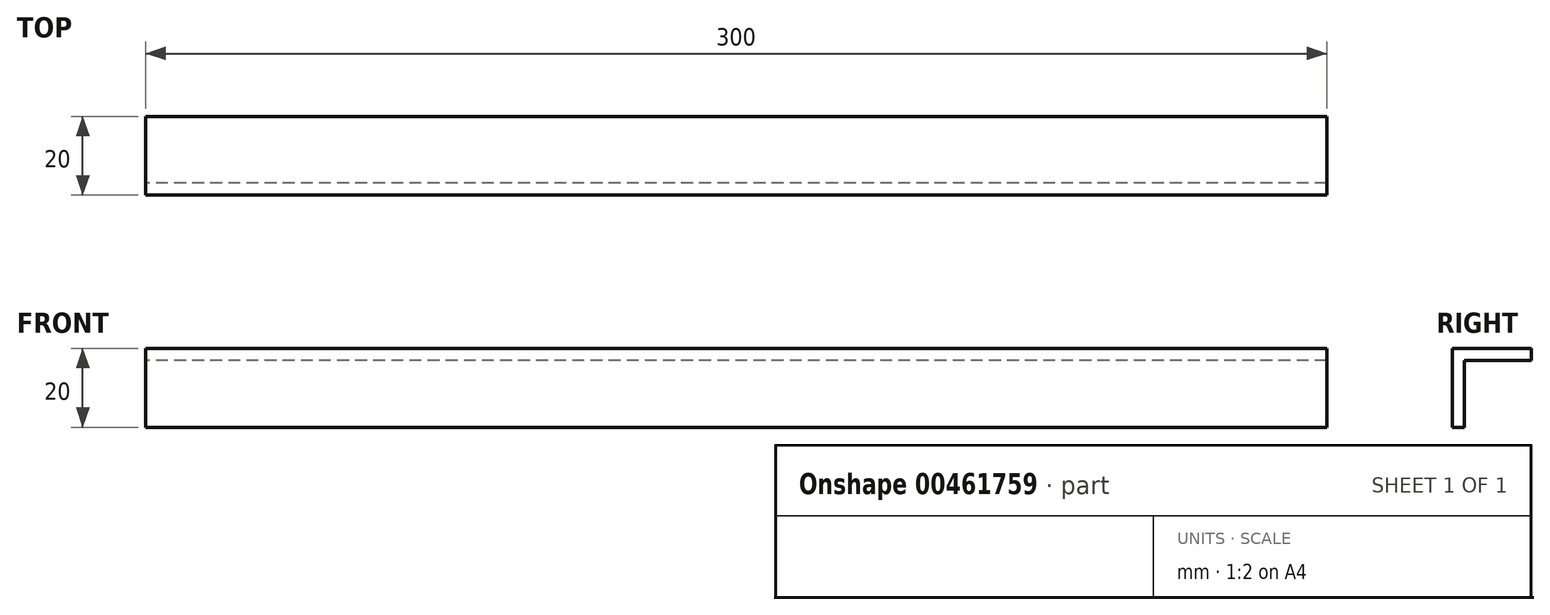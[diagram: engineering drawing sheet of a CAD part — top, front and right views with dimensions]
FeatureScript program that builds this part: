
annotation { "Feature Type Name" : "Feature", "Feature Type Description" : "" }
export const myFeature = defineFeature(function(context is Context, id is Id, definition is map)
    precondition{}
    {
        {
            var Q0;
            Q0=qCreatedBy(makeId("Front.planeOp"),FACE);
            var sketch = newSketch(context, id + "F0", { "sketchPlane" : qUnion([Q0])});
            skLineSegment(sketch, "E0.bottom", {"start": v(0, 0) * mm, "end": v(300, 0) * mm});
            skLineSegment(sketch, "E0.top", {"start": v(0, 20) * mm, "end": v(300, 20) * mm});
            skLineSegment(sketch, "E0.left", {"start": v(0, 0) * mm, "end": v(0, 20) * mm});
            skLineSegment(sketch, "E0.right", {"start": v(300, 0) * mm, "end": v(300, 20) * mm});
            skSolve(sketch);
        }
        {
            var Q0;
            Q0=makeQuery(id+"F0.imprint","IMPRINT",FACE,{"disambiguationData":[TD([[makeQuery(id+"F0.imprint","IMPRINT",EDGE,{"derivedFrom":sQuery(id+"F0.wireOp",EDGE,"E0.bottom")}),1.0]])]});
            var Q1;
            Q1=sQuery(id+"F0.wireOp",EDGE,"E0.top");
            extrude(context, id + "F1", {"entities" : qUnion([Q0]), "surfaceEntities" : qUnion([Q1]), "depth" : 20 * mm});
        }
        {
            var Q0;
            Q0=qCreatedBy(makeId("Right.planeOp"),FACE);
            var sketch = newSketch(context, id + "F2", { "sketchPlane" : qUnion([Q0])});
            skLineSegment(sketch, "E1.bottom", {"start": v(0, 0) * mm, "end": v(-17, 0) * mm});
            skLineSegment(sketch, "E1.top", {"start": v(0, 17) * mm, "end": v(-17, 17) * mm});
            skLineSegment(sketch, "E1.left", {"start": v(0, 0) * mm, "end": v(0, 17) * mm});
            skLineSegment(sketch, "E1.right", {"start": v(-17, 0) * mm, "end": v(-17, 17) * mm});
            skSolve(sketch);
        }
        {
            var Q0;
            Q0 = qSketchRegion(id + "F2", true);
            extrude(context, id + "F3", {"entities" : qUnion([Q0]), "operationType" : NewBodyOperationType.REMOVE, "depth" : 300 * mm});
        }
    });
